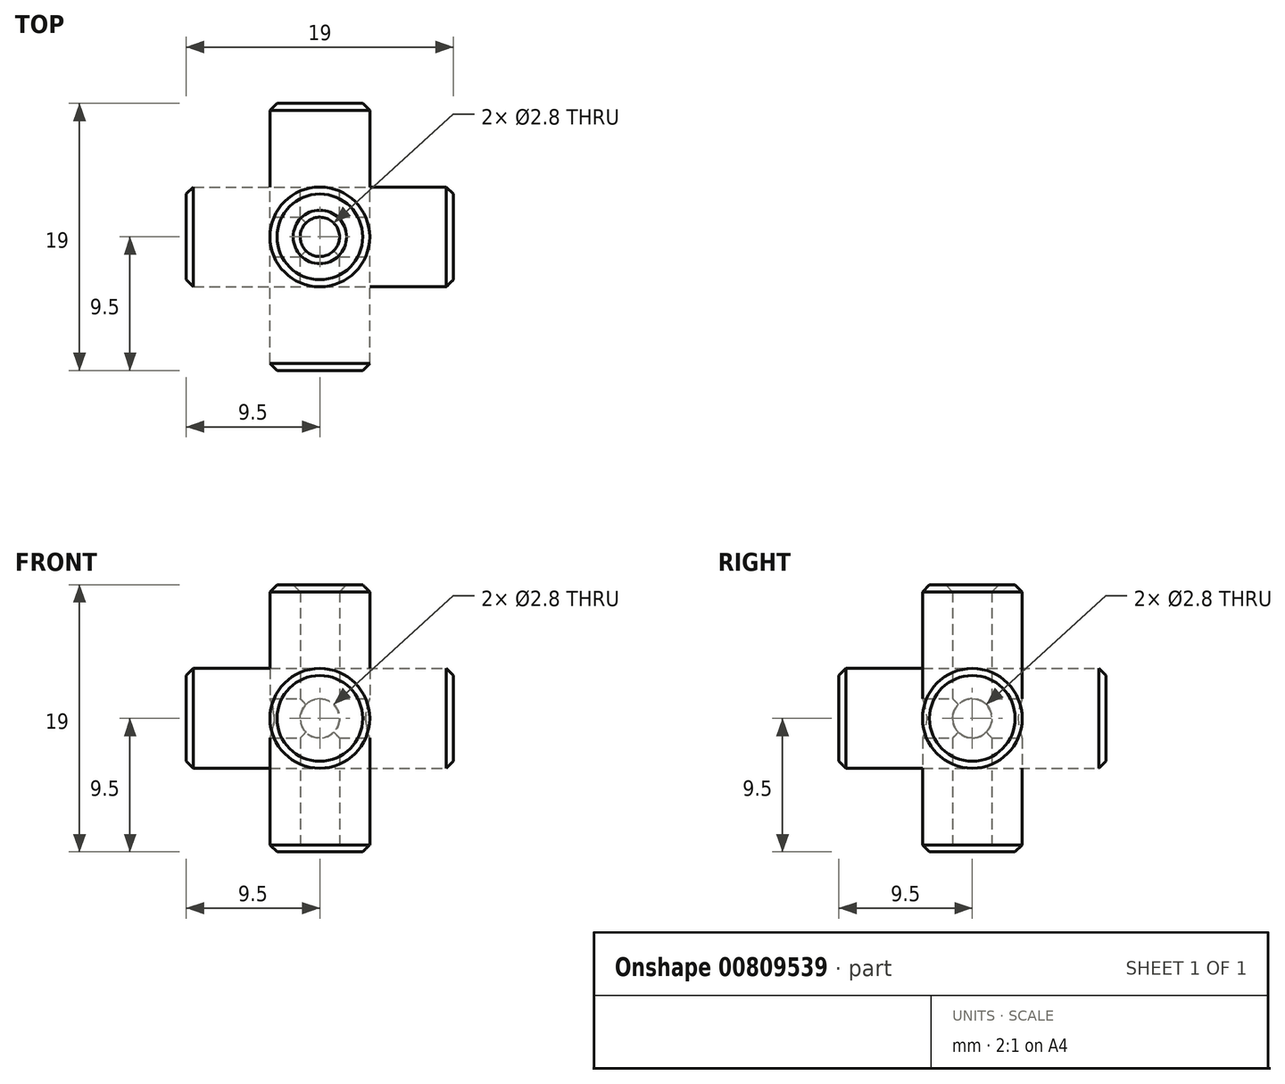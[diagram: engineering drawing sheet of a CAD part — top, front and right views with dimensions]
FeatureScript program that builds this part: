
annotation { "Feature Type Name" : "Feature", "Feature Type Description" : "" }
export const myFeature = defineFeature(function(context is Context, id is Id, definition is map)
    precondition{}
    {
        {
            var Q0;
            Q0=qCreatedBy(makeId("Front.planeOp"),FACE);
            var sketch = newSketch(context, id + "F0", { "sketchPlane" : qUnion([Q0])});
            skCircle(sketch, "E0", {"center": v(0, 0) * mm, "radius": 3.55 * mm});
            skSolve(sketch);
        }
        {
            var Q0;
            Q0 = qSketchRegion(id + "F0", true);
            extrude(context, id + "F1", {"entities" : qUnion([Q0]), "endBound" : BoundingType.SYMMETRIC, "depth" : 19 * mm, "offsetDistance" : 25 * mm});
        }
        {
            var Q0;
            Q0=qCreatedBy(makeId("Front.planeOp"),FACE);
            var sketch = newSketch(context, id + "F2", { "sketchPlane" : qUnion([Q0])});
            skCircle(sketch, "E1", {"center": v(0, 0) * mm, "radius": 1.4 * mm});
            skSolve(sketch);
        }
        {
            var Q0;
            Q0 = qSketchRegion(id + "F2", true);
            extrude(context, id + "F3", {"entities" : qUnion([Q0]), "endBound" : BoundingType.SYMMETRIC, "depth" : 20 * mm, "offsetDistance" : 25 * mm});
        }
        {
            var Q0;
            Q0=qCreatedBy(makeId("Front.planeOp"),FACE);
            var sketch = newSketch(context, id + "F4", { "sketchPlane" : qUnion([Q0])});
            skLineSegment(sketch, "E2.bottom", {"start": v(0, 0) * mm, "end": v(-10, 0) * mm});
            skLineSegment(sketch, "E2.top", {"start": v(0, 10) * mm, "end": v(-10, 10) * mm});
            skLineSegment(sketch, "E2.left", {"start": v(0, 0) * mm, "end": v(0, 10) * mm});
            skLineSegment(sketch, "E2.right", {"start": v(-10, 0) * mm, "end": v(-10, 10) * mm});
            skSolve(sketch);
        }
        {
            var Q0;
            Q0 = qSketchRegion(id + "F4", true);
            extrude(context, id + "F5", {"entities" : qUnion([Q0]), "depth" : 10 * mm, "offsetDistance" : 25 * mm});
        }
        {
            var Q0;
            Q0=qCreatedBy(makeId("Origin.pointOp"),VERTEX);
            var Q1;
            Q1=makeQuery(id+"F5.opExtrude","CAP_VERTEX",VERTEX,{"disambiguationData":[OSD([sQuery(id+"F4.wireOp",EDGE,"E2.top"),sQuery(id+"F4.wireOp",EDGE,"E2.right")])],"isStart":false});
            var Q2;
            Q2=makeQuery(id+"F5.opExtrude","CAP_VERTEX",VERTEX,{"disambiguationData":[OSD([sQuery(id+"F4.wireOp",EDGE,"E2.bottom"),sQuery(id+"F4.wireOp",EDGE,"E2.right")])],"isStart":false});
            cPlane(context, id + "F6", {"entities" : qUnion([Q0, Q1, Q2]), "cplaneType" : CPlaneType.THREE_POINT, "offset" : 25 * mm, "width" : 150 * mm, "height" : 150 * mm});
        }
        {
            var Q0;
            Q0=qCreatedBy(id+"F6.planeOp",FACE);
            var sketch = newSketch(context, id + "F7", { "sketchPlane" : qUnion([Q0])});
            skLineSegment(sketch, "E3", {"start": v(0, 0) * mm, "end": v(14.14, 10) * mm});
            skSolve(sketch);
        }
        {
            var Q0;
            Q0=makeQuery(id+"F5.opExtrude","SWEPT_BODY",BODY,{"disambiguationData":[OSD([sQuery(id+"F4.wireOp",EDGE,"E2.bottom"),sQuery(id+"F4.wireOp",EDGE,"E2.top"),sQuery(id+"F4.wireOp",EDGE,"E2.left"),sQuery(id+"F4.wireOp",EDGE,"E2.right")])]});
            deleteBodies(context, id + "F8", {"entities" : qUnion([Q0])});
        }
        {
            var Q0;
            Q0=makeQuery(id+"F3.opExtrude","SWEPT_BODY",BODY,{"disambiguationData":[OSD([sQuery(id+"F2.wireOp",EDGE,"E1")])]});
            var Q1;
            Q1=makeQuery(id+"F1.opExtrude","SWEPT_BODY",BODY,{"disambiguationData":[OSD([sQuery(id+"F0.wireOp",EDGE,"E0")])]});
            var Q2;
            Q2=sQuery(id+"F7.wireOp",EDGE,"E3");
            circularPattern(context, id + "F9", {"entities" : qUnion([Q0, Q1]), "axis" : qUnion([Q2]), "angle" : 360 * degree, "instanceCount" : 3, "equalSpace" : true});
        }
        {
            var Q0;
            Q0=makeQuery(id+"F3.opExtrude","SWEPT_BODY",BODY,{"disambiguationData":[OSD([sQuery(id+"F2.wireOp",EDGE,"E1")])]});
            var Q1;
            Q1=makeQuery(id+"F9.opPattern","COPY",BODY,{"derivedFrom":makeQuery(id+"F3.opExtrude","SWEPT_BODY",BODY,{"disambiguationData":[OSD([sQuery(id+"F2.wireOp",EDGE,"E1")])]}),"instanceName":"1"});
            var Q2;
            Q2=makeQuery(id+"F9.opPattern","COPY",BODY,{"derivedFrom":makeQuery(id+"F3.opExtrude","SWEPT_BODY",BODY,{"disambiguationData":[OSD([sQuery(id+"F2.wireOp",EDGE,"E1")])]}),"instanceName":"2"});
            var Q3;
            Q3=makeQuery(id+"F9.opPattern","COPY",BODY,{"derivedFrom":makeQuery(id+"F1.opExtrude","SWEPT_BODY",BODY,{"disambiguationData":[OSD([sQuery(id+"F0.wireOp",EDGE,"E0")])]}),"instanceName":"1"});
            booleanBodies(context, id + "F10", {"operationType" : BooleanOperationType.SUBTRACTION, "tools" : qUnion([Q0, Q1, Q2]), "targets" : qUnion([Q3])});
        }
        {
            var Q0;
            Q0=makeQuery(id+"F1.opExtrude","CAP_FACE",FACE,{"disambiguationData":[OSD([sQuery(id+"F0.wireOp",EDGE,"E0")])],"isStart":true});
            var Q1;
            Q1=makeQuery(id+"F9.opPattern","COPY",FACE,{"derivedFrom":makeQuery(id+"F1.opExtrude","CAP_FACE",FACE,{"disambiguationData":[OSD([sQuery(id+"F0.wireOp",EDGE,"E0")])],"isStart":true}),"instanceName":"2"});
            var Q2;
            Q2=makeQuery(id+"F9.opPattern","COPY",FACE,{"derivedFrom":makeQuery(id+"F1.opExtrude","CAP_FACE",FACE,{"disambiguationData":[OSD([sQuery(id+"F0.wireOp",EDGE,"E0")])],"isStart":false}),"instanceName":"1"});
            var Q3;
            Q3=makeQuery(id+"F1.opExtrude","CAP_FACE",FACE,{"disambiguationData":[OSD([sQuery(id+"F0.wireOp",EDGE,"E0")])],"isStart":false});
            var Q4;
            Q4=makeQuery(id+"F9.opPattern","COPY",FACE,{"derivedFrom":makeQuery(id+"F1.opExtrude","CAP_FACE",FACE,{"disambiguationData":[OSD([sQuery(id+"F0.wireOp",EDGE,"E0")])],"isStart":false}),"instanceName":"2"});
            var Q5;
            Q5=makeQuery(id+"F9.opPattern","COPY",EDGE,{"derivedFrom":makeQuery(id+"F1.opExtrude","CAP_EDGE",EDGE,{"disambiguationData":[OSD([sQuery(id+"F0.wireOp",EDGE,"E0")])],"isStart":true}),"instanceName":"1"});
            chamfer(context, id + "F11", {"entities" : qUnion([Q0, Q1, Q2, Q3, Q4, Q5]), "width" : 0.5 * mm, "tangentPropagation" : true});
        }
    });
